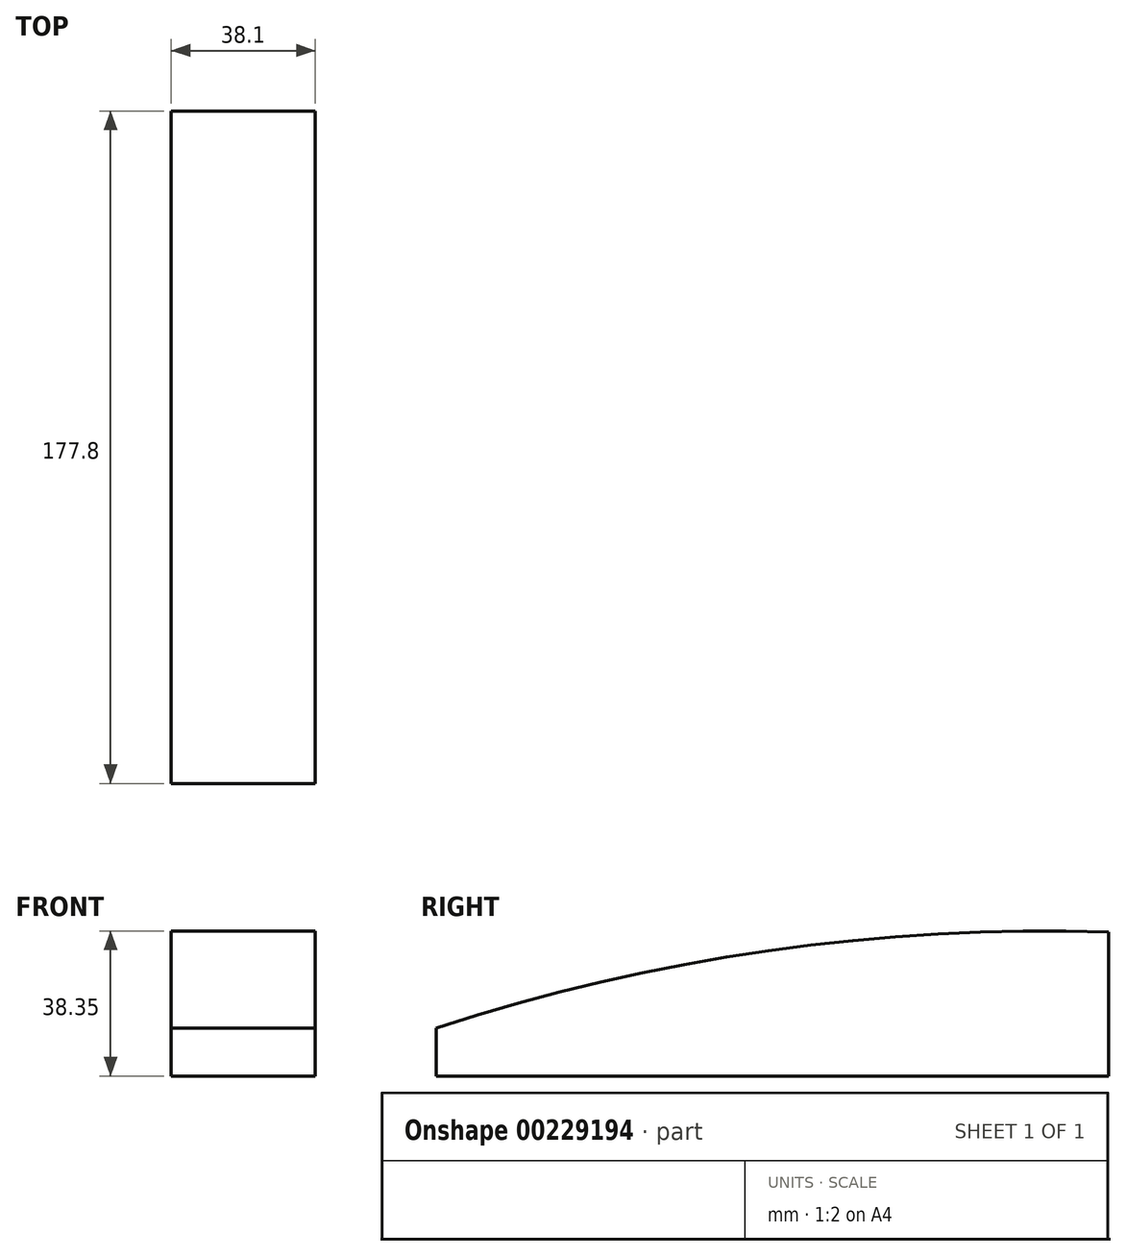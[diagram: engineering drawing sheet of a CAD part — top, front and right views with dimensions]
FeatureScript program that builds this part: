
annotation { "Feature Type Name" : "Feature", "Feature Type Description" : "" }
export const myFeature = defineFeature(function(context is Context, id is Id, definition is map)
    precondition{}
    {
        {
            var Q0;
            Q0=qCreatedBy(makeId("Right.planeOp"),FACE);
            var sketch = newSketch(context, id + "F0", { "sketchPlane" : qUnion([Q0])});
            skLineSegment(sketch, "E0", {"start": v(-73.92, 0) * mm, "end": v(103.88, 0) * mm});
            skLineSegment(sketch, "E1", {"start": v(-73.92, 12.7) * mm, "end": v(-73.92, 0) * mm});
            skLineSegment(sketch, "E2", {"start": v(103.88, 38.1) * mm, "end": v(103.88, 0) * mm});
            skArc(sketch, "E3", {"start": v(103.88, 38.1) * mm, "mid": v(13.88, 33.12) * mm, "end": v(-73.92, 12.7) * mm});
            skSolve(sketch);
        }
        {
            var Q0;
            Q0 = qSketchRegion(id + "F0", true);
            extrude(context, id + "F1", {"entities" : qUnion([Q0]), "depth" : 38.1 * mm});
        }
    });
